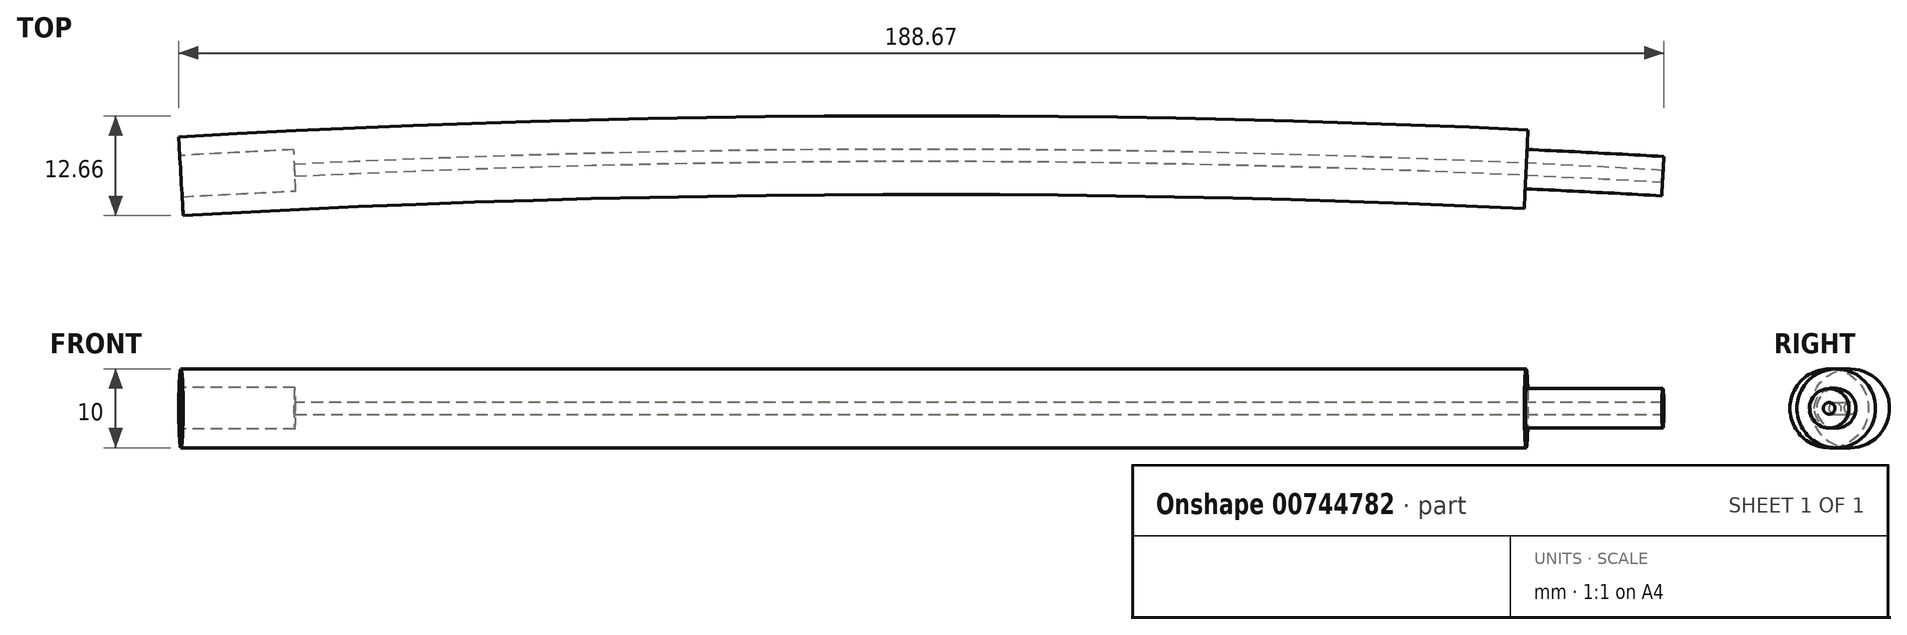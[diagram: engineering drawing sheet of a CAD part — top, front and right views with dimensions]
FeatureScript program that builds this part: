
annotation { "Feature Type Name" : "Feature", "Feature Type Description" : "" }
export const myFeature = defineFeature(function(context is Context, id is Id, definition is map)
    precondition{}
    {
        {
            var Q0;
            Q0=qCreatedBy(makeId("Top.planeOp"),FACE);
            var sketch = newSketch(context, id + "F0", { "sketchPlane" : qUnion([Q0])});
            skLineSegment(sketch, "E0", {"start": v(93.84, 1652.55) * mm, "end": v(-93.84, 1652.55) * mm, "construction": true});
            skLineSegment(sketch, "E1", {"start": v(-93.84, 1652.55) * mm, "end": v(0, 0) * mm, "construction": true});
            skLineSegment(sketch, "E2", {"start": v(93.84, 1652.55) * mm, "end": v(0, 0) * mm, "construction": true});
            skArc(sketch, "E3", {"start": v(93.84, 1652.55) * mm, "mid": v(0, 1655.21) * mm, "end": v(-93.84, 1652.55) * mm});
            skArc(sketch, "E4.0", {"start": v(94.4, 1662.53) * mm, "mid": v(0, 1665.21) * mm, "end": v(-94.4, 1662.53) * mm});
            skLineSegment(sketch, "E5", {"start": v(-93.84, 1652.55) * mm, "end": v(-94.4, 1662.53) * mm});
            skLineSegment(sketch, "E6", {"start": v(93.84, 1652.55) * mm, "end": v(94.4, 1662.53) * mm});
            skSolve(sketch);
        }
        {
            var Q0;
            Q0=makeQuery(id+"F0.imprint","IMPRINT",FACE,{"disambiguationData":[TD([[makeQuery(id+"F0.imprint","IMPRINT",EDGE,{"derivedFrom":sQuery(id+"F0.wireOp",EDGE,"E3")}),-1.0]])]});
            extrude(context, id + "F1", {"entities" : qUnion([Q0]), "depth" : 10 * mm, "offsetDistance" : 25 * mm});
        }
        {
            var Q0;
            Q0=qCreatedBy(makeId("Top.planeOp"),FACE);
            cPlane(context, id + "F2", {"entities" : qUnion([Q0]), "cplaneType" : CPlaneType.OFFSET, "offset" : 5 * mm, "width" : 150 * mm, "height" : 150 * mm});
        }
        {
            var Q0;
            Q0=qCreatedBy(id+"F2.planeOp",FACE);
            var sketch = newSketch(context, id + "F3", { "sketchPlane" : qUnion([Q0])});
            skCircle(sketch, "E7", {"center": v(0, 0) * mm, "radius": 1655.21 * mm, "construction": true});
            skArc(sketch, "E8", {"start": v(94.12, 1657.54) * mm, "mid": v(0, 1660.21) * mm, "end": v(-94.12, 1657.54) * mm});
            skSolve(sketch);
        }
        {
            var Q0;
            Q0=makeQuery(id+"F1.opExtrude","SWEPT_FACE",FACE,{"disambiguationData":[OSD([sQuery(id+"F0.wireOp",EDGE,"E5")])]});
            var sketch = newSketch(context, id + "F4", { "sketchPlane" : qUnion([Q0])});
            skCircle(sketch, "E9", {"center": v(-1660.21, 5) * mm, "radius": 5 * mm});
            skCircle(sketch, "E10", {"center": v(-1660.21, 5) * mm, "radius": 0.75 * mm});
            skSolve(sketch);
        }
        {
            var Q0;
            Q0 = qSketchRegion(id + "F4", true);
            var Q1;
            Q1 = qConstructionFilter(qBodyType(qCreatedBy(id + "F3" ,EDGE), BodyType.WIRE), ConstructionObject.NO);
            sweep(context, id + "F5", {"operationType" : NewBodyOperationType.INTERSECT, "profiles" : qUnion([Q0]), "path" : qUnion([Q1])});
        }
        {
            var Q0;
            Q0=qCreatedBy(id+"F2.planeOp",FACE);
            var sketch = newSketch(context, id + "F6", { "sketchPlane" : qUnion([Q0])});
            skArc(sketch, "E11", {"start": v(-94.12, 1657.54) * mm, "mid": v(-86.89, 1657.94) * mm, "end": v(-79.65, 1658.3) * mm});
            skLineSegment(sketch, "E12", {"start": v(-94.12, 1657.54) * mm, "end": v(0, 0) * mm, "construction": true});
            skLineSegment(sketch, "E13", {"start": v(0, 0) * mm, "end": v(-79.65, 1658.3) * mm, "construction": true});
            skSolve(sketch);
        }
        {
            var Q0;
            Q0=makeQuery(id+"F1.opExtrude","SWEPT_FACE",FACE,{"disambiguationData":[OSD([sQuery(id+"F0.wireOp",EDGE,"E5")])]});
            var sketch = newSketch(context, id + "F7", { "sketchPlane" : qUnion([Q0])});
            skCircle(sketch, "E14", {"center": v(-1660.21, 5) * mm, "radius": 2.62 * mm});
            skSolve(sketch);
        }
        {
            var Q0;
            Q0 = qSketchRegion(id + "F7", true);
            var Q1;
            Q1 = qConstructionFilter(qBodyType(qCreatedBy(id + "F6" ,EDGE), BodyType.WIRE), ConstructionObject.NO);
            sweep(context, id + "F8", {"operationType" : NewBodyOperationType.REMOVE, "profiles" : qUnion([Q0]), "path" : qUnion([Q1])});
        }
        {
            var Q0;
            Q0=qCreatedBy(id+"F2.planeOp",FACE);
            var sketch = newSketch(context, id + "F9", { "sketchPlane" : qUnion([Q0])});
            skArc(sketch, "E15", {"start": v(94.12, 1657.54) * mm, "mid": v(85.44, 1658.01) * mm, "end": v(76.76, 1658.44) * mm});
            skLineSegment(sketch, "E16", {"start": v(94.12, 1657.54) * mm, "end": v(0, 0) * mm, "construction": true});
            skLineSegment(sketch, "E17", {"start": v(0, 0) * mm, "end": v(76.76, 1658.44) * mm, "construction": true});
            skSolve(sketch);
        }
        {
            var Q0;
            Q0=makeQuery(id+"F1.opExtrude","SWEPT_FACE",FACE,{"disambiguationData":[OSD([sQuery(id+"F0.wireOp",EDGE,"E6")])]});
            var sketch = newSketch(context, id + "F10", { "sketchPlane" : qUnion([Q0])});
            skCircle(sketch, "E18", {"center": v(1660.21, 5) * mm, "radius": 2.5 * mm});
            skCircle(sketch, "E19", {"center": v(1660.21, 5) * mm, "radius": 5 * mm});
            skSolve(sketch);
        }
        {
            var Q0;
            Q0 = qSketchRegion(id + "F10", true);
            var Q1;
            Q1 = qConstructionFilter(qBodyType(qCreatedBy(id + "F9" ,EDGE), BodyType.WIRE), ConstructionObject.NO);
            sweep(context, id + "F11", {"operationType" : NewBodyOperationType.REMOVE, "profiles" : qUnion([Q0]), "path" : qUnion([Q1])});
        }
    });
